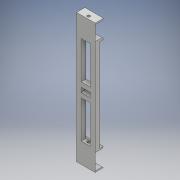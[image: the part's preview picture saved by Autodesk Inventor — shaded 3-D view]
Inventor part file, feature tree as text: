
AUTODESK INVENTOR PART (.ipt)
format: ipt  version: 2018 (Build 220112000, 112)  size: 446,464 bytes
history: native  units: mm
features: extrude x7, sketch x7, chamfer x5
ambient origin geometry x8: Origin, YZ Plane, XZ Plane, XY Plane, X Axis, Y Axis, Z Axis, Center Point
bodies: Solid1 (feature_tree)
feature tree (19):
  extrude  "Extrusion1"  Depth=140.0mm
  extrude  "Extrusion2"  Depth=20.0mm
  extrude  "Extrusion3"  Depth=4.0mm TaperAngle=0.0deg
  extrude  "Extrusion4"  Depth=10.0mm
  extrude  "Extrusion5"  Depth=10.0mm
  chamfer  "Chamfer1"  Distance=5.0mm
  chamfer  "Chamfer2"  Distance=50.0mm
  chamfer  "Chamfer3"  Distance=2.0mm
  extrude  "Extrusion8"  Depth=10.0mm
  extrude  "Extrusion9"  Depth=10.0mm
  chamfer  "Chamfer4"  Distance=5.0mm
  chamfer  "Chamfer5"  Distance=5.0mm
  sketch  "Sketch1"  dims[d0=20.0mm d1=140.0mm]
  sketch  "Sketch2"  dims[d2=5.0mm d3=0.0mm d4=20.0mm]
  sketch  "Sketch3"  dims[d5=20.0mm d6=4.0mm d7=0.0mm]
  sketch  "Sketch4"  dims[d8=5.0mm d9=10.0mm]
  sketch  "Sketch5"  dims[d10=5.0mm d11=10.0mm d12=5.0mm d13=0.0mm d15=50.0mm d16=0.0mm]
  sketch  "Sketch8"  dims[d17=2.0mm]
  sketch  "Sketch9"  dims[d18=5.0mm d19=2.0mm d21=5.0mm d22=2.5mm d23=5.0mm d24=5.0mm d25=5.0mm d26=10.0mm d27=0.0mm d28=4.0mm d29=2.0mm d30=45.0deg d31=5.0mm d32=2.0mm d33=45.0deg d34=3.5mm d35=2.0mm d36=45.0deg d46=2.0mm d53=3.0mm d54=3.0mm d55=30.0mm d56=0.0mm d57=5.0mm d58=30.0mm d59=0.0mm d60=2.0mm d61=3.0mm d62=2.0mm d63=45.0deg d64=3.0mm d65=2.0mm d66=45.0deg]
